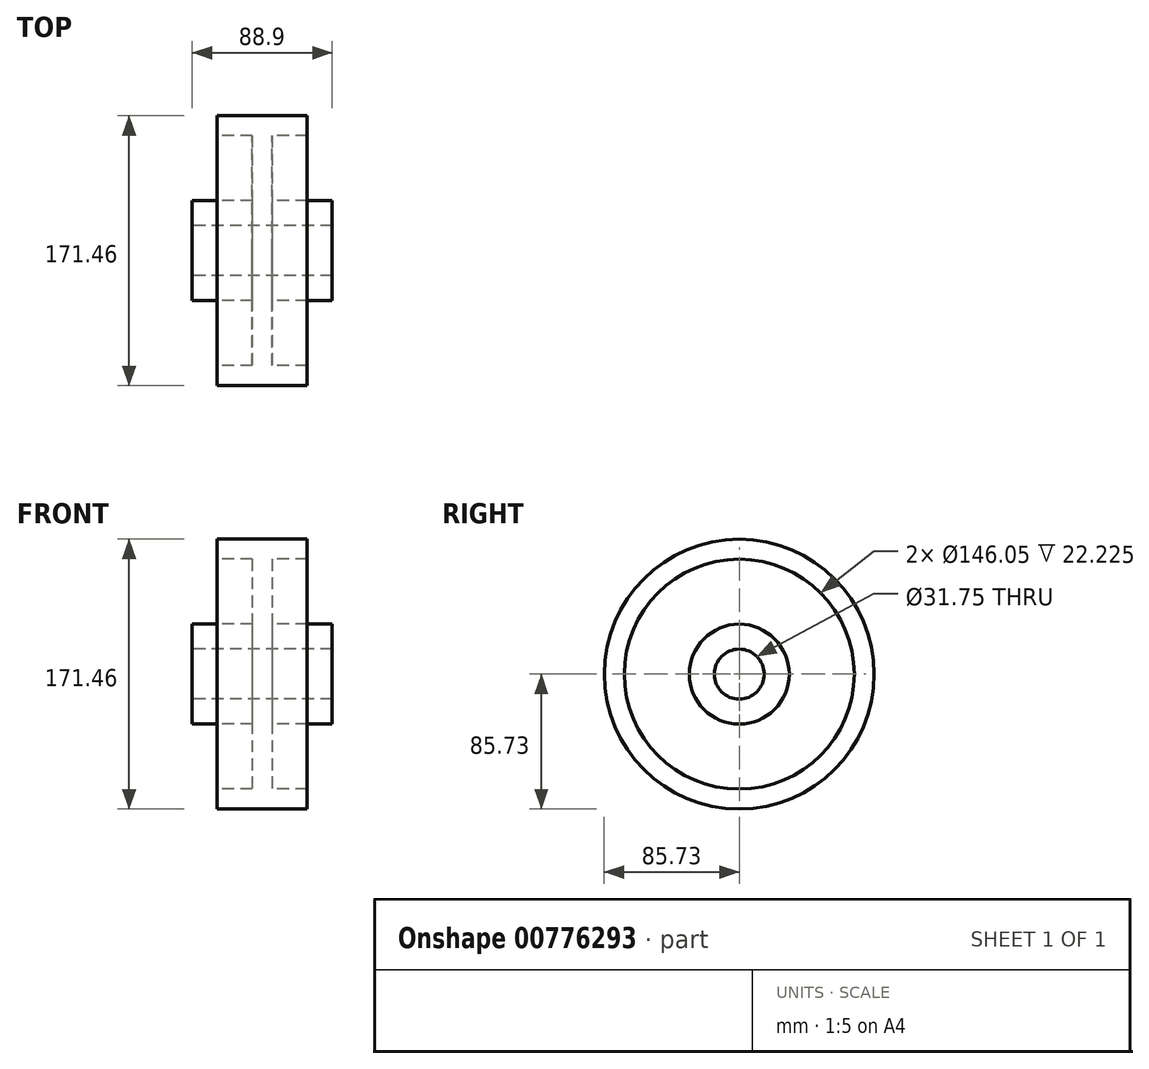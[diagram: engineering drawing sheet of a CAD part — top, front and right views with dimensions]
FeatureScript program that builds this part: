
annotation { "Feature Type Name" : "Feature", "Feature Type Description" : "" }
export const myFeature = defineFeature(function(context is Context, id is Id, definition is map)
    precondition{}
    {
        {
            var Q0;
            Q0=qCreatedBy(makeId("Front.planeOp"),FACE);
            var sketch = newSketch(context, id + "F0", { "sketchPlane" : qUnion([Q0])});
            skLineSegment(sketch, "E0", {"start": v(-129.31, 0) * mm, "end": v(120.37, 0) * mm, "construction": true});
            skLineSegment(sketch, "E1", {"start": v(0, 0) * mm, "end": v(0, 96.33) * mm, "construction": true});
            skLineSegment(sketch, "E2", {"start": v(-44.45, 15.88) * mm, "end": v(44.45, 15.88) * mm});
            skLineSegment(sketch, "E3", {"start": v(44.45, 31.75) * mm, "end": v(6.35, 31.75) * mm});
            skLineSegment(sketch, "E4", {"start": v(6.35, 31.75) * mm, "end": v(6.35, 73.03) * mm});
            skLineSegment(sketch, "E5", {"start": v(6.35, 73.03) * mm, "end": v(28.58, 73.03) * mm});
            skLineSegment(sketch, "E6", {"start": v(28.58, 73.03) * mm, "end": v(28.58, 85.73) * mm});
            skLineSegment(sketch, "E7", {"start": v(28.58, 85.73) * mm, "end": v(-28.57, 85.73) * mm});
            skLineSegment(sketch, "E8", {"start": v(-28.58, 85.73) * mm, "end": v(-28.58, 73.03) * mm});
            skLineSegment(sketch, "E9", {"start": v(-28.58, 73.03) * mm, "end": v(-6.35, 73.03) * mm});
            skLineSegment(sketch, "E10", {"start": v(-6.35, 73.03) * mm, "end": v(-6.35, 31.75) * mm});
            skLineSegment(sketch, "E11", {"start": v(-6.35, 31.75) * mm, "end": v(-44.45, 31.75) * mm});
            skLineSegment(sketch, "E12", {"start": v(-44.45, 31.75) * mm, "end": v(-44.45, 15.88) * mm});
            skLineSegment(sketch, "E13", {"start": v(44.45, 31.75) * mm, "end": v(44.45, 15.88) * mm});
            skSolve(sketch);
        }
        {
            var Q0;
            Q0 = qSketchRegion(id + "F0", true);
            var Q1;
            Q1=sQuery(id+"F0.wireOp",EDGE,"E0");
            revolve(context, id + "F1", {"surfaceOperationType" : NewSurfaceOperationType.NEW, "entities" : qUnion([Q0]), "axis" : qUnion([Q1]), "revolveType" : RevolveType.FULL});
        }
    });
